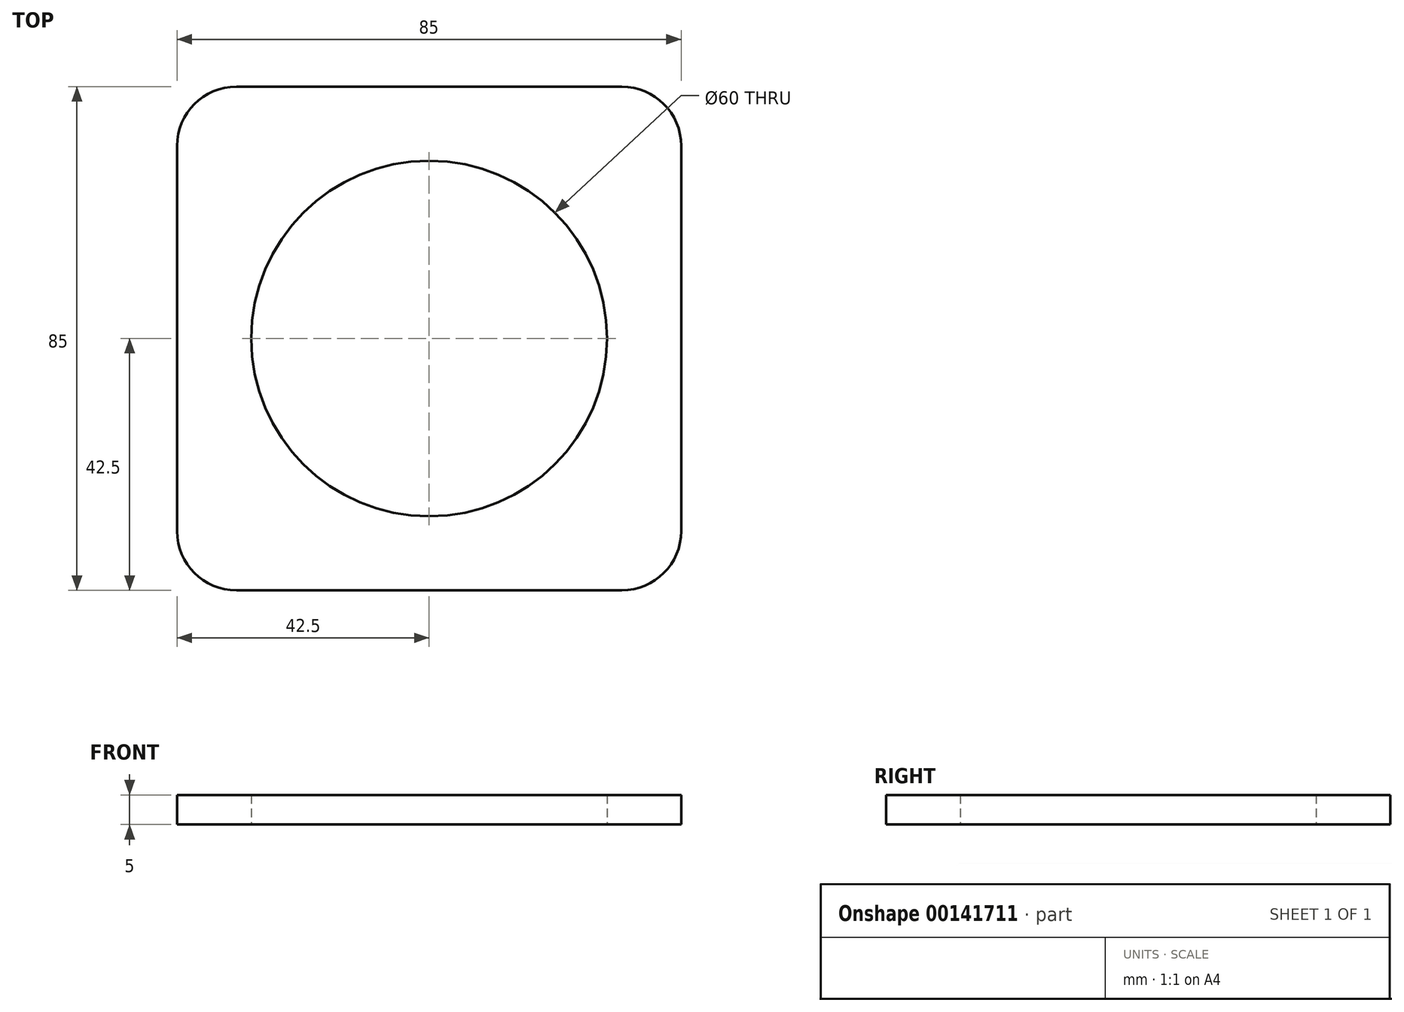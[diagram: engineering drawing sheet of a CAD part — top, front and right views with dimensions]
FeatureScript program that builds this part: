
annotation { "Feature Type Name" : "Feature", "Feature Type Description" : "" }
export const myFeature = defineFeature(function(context is Context, id is Id, definition is map)
    precondition{}
    {
        {
            var Q0;
            Q0=qCreatedBy(makeId("Top.planeOp"),FACE);
            var sketch = newSketch(context, id + "F0", { "sketchPlane" : qUnion([Q0])});
            skLineSegment(sketch, "E0.bottom", {"start": v(-32.5, 42.5) * mm, "end": v(32.5, 42.5) * mm});
            skLineSegment(sketch, "E0.top", {"start": v(-32.5, -42.5) * mm, "end": v(32.5, -42.5) * mm});
            skLineSegment(sketch, "E0.left", {"start": v(-42.5, 32.5) * mm, "end": v(-42.5, -32.5) * mm});
            skLineSegment(sketch, "E0.right", {"start": v(42.5, 32.5) * mm, "end": v(42.5, -32.5) * mm});
            skCircle(sketch, "E1", {"center": v(0, 0) * mm, "radius": 30 * mm});
            skPoint(sketch, "E2.visualSharp", {"position": v(-42.5, 42.5) * mm});
            skArc(sketch, "E2.filletArc", {"start": v(-32.5, 42.5) * mm, "mid": v(-39.57, 39.57) * mm, "end": v(-42.5, 32.5) * mm});
            skPoint(sketch, "E3.visualSharp", {"position": v(42.5, 42.5) * mm});
            skArc(sketch, "E3.filletArc", {"start": v(42.5, 32.5) * mm, "mid": v(39.57, 39.57) * mm, "end": v(32.5, 42.5) * mm});
            skPoint(sketch, "E4.visualSharp", {"position": v(42.5, -42.5) * mm});
            skArc(sketch, "E4.filletArc", {"start": v(32.5, -42.5) * mm, "mid": v(39.57, -39.57) * mm, "end": v(42.5, -32.5) * mm});
            skPoint(sketch, "E5.visualSharp", {"position": v(-42.5, -42.5) * mm});
            skArc(sketch, "E5.filletArc", {"start": v(-42.5, -32.5) * mm, "mid": v(-39.57, -39.57) * mm, "end": v(-32.5, -42.5) * mm});
            skSolve(sketch);
        }
        {
            var Q0;
            Q0=qSketchRegion(id+"F0",true);
            extrude(context, id + "F1", {"entities" : qUnion([Q0]), "depth" : 5 * mm});
        }
    });
